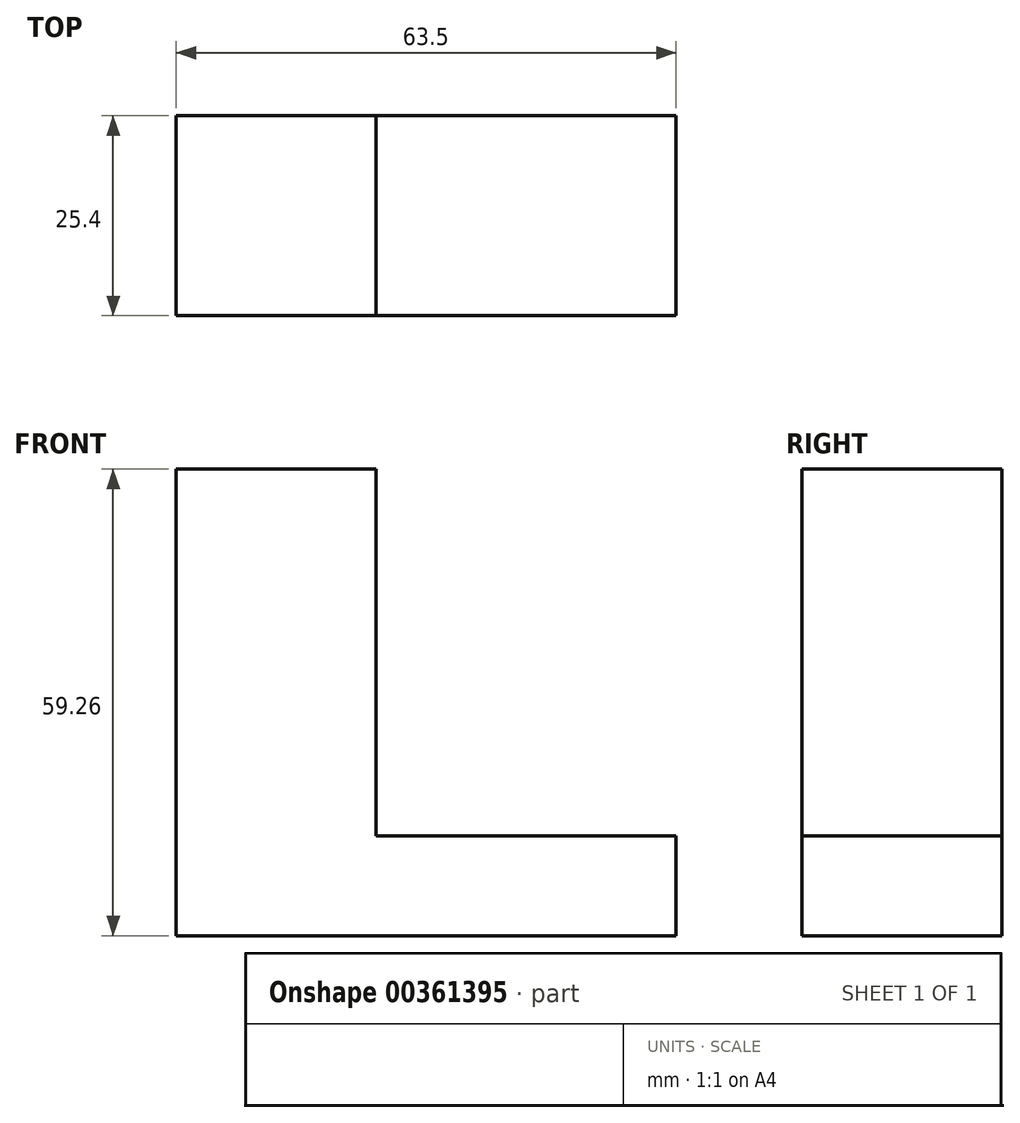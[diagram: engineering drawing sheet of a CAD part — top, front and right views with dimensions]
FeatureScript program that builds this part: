
annotation { "Feature Type Name" : "Feature", "Feature Type Description" : "" }
export const myFeature = defineFeature(function(context is Context, id is Id, definition is map)
    precondition{}
    {
        {
            var Q0;
            Q0=qCreatedBy(makeId("Front.planeOp"),FACE);
            var sketch = newSketch(context, id + "F0", { "sketchPlane" : qUnion([Q0])});
            skLineSegment(sketch, "E0", {"start": v(-31.63, 22.87) * mm, "end": v(-31.63, -36.4) * mm});
            skLineSegment(sketch, "E1", {"start": v(-31.63, -36.4) * mm, "end": v(31.87, -36.4) * mm});
            skLineSegment(sketch, "E2", {"start": v(31.87, -36.4) * mm, "end": v(31.87, -23.7) * mm});
            skLineSegment(sketch, "E3", {"start": v(31.87, -23.7) * mm, "end": v(-6.23, -23.7) * mm});
            skLineSegment(sketch, "E4", {"start": v(-6.23, -23.7) * mm, "end": v(-6.23, 22.87) * mm});
            skLineSegment(sketch, "E5", {"start": v(-6.23, 22.87) * mm, "end": v(-31.63, 22.87) * mm});
            skSolve(sketch);
        }
        {
            var Q0;
            Q0 = qSketchRegion(id + "F0", true);
            extrude(context, id + "F1", {"entities" : qUnion([Q0]), "depth" : 25.4 * mm});
        }
    });
